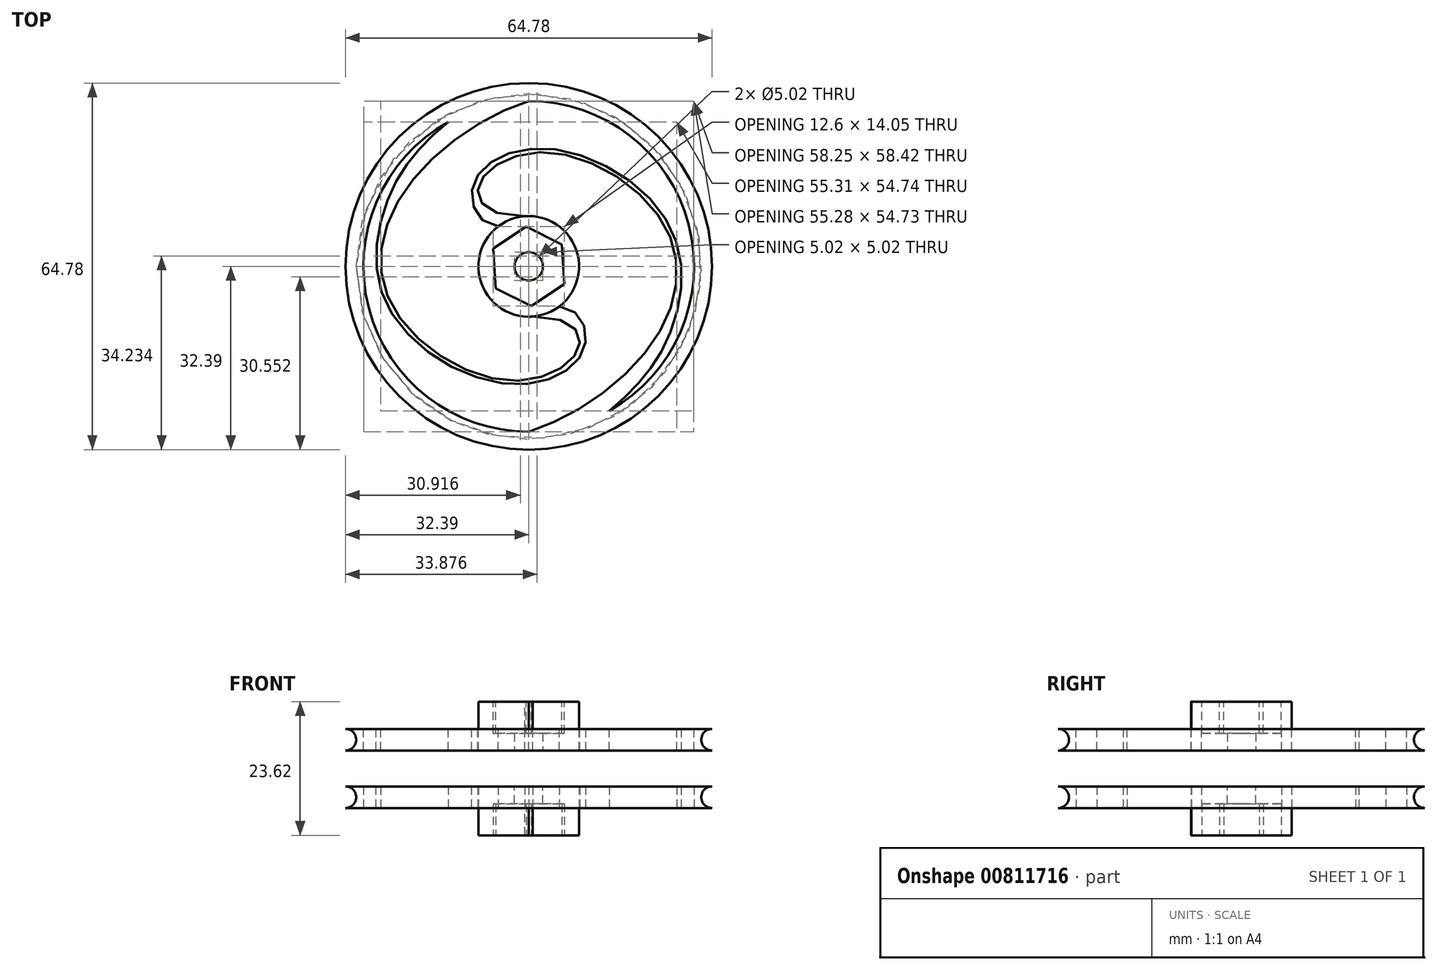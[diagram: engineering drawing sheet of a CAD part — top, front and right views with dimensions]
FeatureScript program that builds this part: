
annotation { "Feature Type Name" : "Feature", "Feature Type Description" : "" }
export const myFeature = defineFeature(function(context is Context, id is Id, definition is map)
    precondition{}
    {
        {
            var Q0;
            Q0=qCreatedBy(makeId("Front.planeOp"),FACE);
            var sketch = newSketch(context, id + "F0", { "sketchPlane" : qUnion([Q0])});
            skLineSegment(sketch, "E0.bottom", {"start": v(-32.39, 0) * mm, "end": v(0, 0) * mm, "construction": true});
            skLineSegment(sketch, "E0.top", {"start": v(-32.39, 1.9) * mm, "end": v(0, 1.9) * mm});
            skLineSegment(sketch, "E0.left", {"start": v(-32.39, 0) * mm, "end": v(-32.39, 1.9) * mm, "construction": true});
            skLineSegment(sketch, "E0.right", {"start": v(0, 0) * mm, "end": v(0, 1.9) * mm});
            skArc(sketch, "E1", {"start": v(-30.48, 0) * mm, "mid": v(-31.04, 1.35) * mm, "end": v(-32.39, 1.9) * mm});
            skArc(sketch, "E2.MirrorCS", {"start": v(-30.48, 0) * mm, "mid": v(-31.04, -1.35) * mm, "end": v(-32.39, -1.9) * mm});
            skLineSegment(sketch, "E3.MirrorCS", {"start": v(-32.39, -1.9) * mm, "end": v(0, -1.9) * mm});
            skLineSegment(sketch, "E4.MirrorCS", {"start": v(0, 0) * mm, "end": v(0, -1.9) * mm});
            skSolve(sketch);
        }
        {
            var Q0;
            Q0=qCreatedBy(makeId("Top.planeOp"),FACE);
            var sketch = newSketch(context, id + "F1", { "sketchPlane" : qUnion([Q0])});
            skCircle(sketch, "E5", {"center": v(0, 0) * mm, "radius": 30.48 * mm});
            skCircle(sketch, "E6", {"center": v(0, 0) * mm, "radius": 29.21 * mm});
            skCircle(sketch, "E7", {"center": v(0, 0) * mm, "radius": 8.9 * mm});
            skLineSegment(sketch, "E8", {"start": v(0, 0) * mm, "end": v(-39.84, 0) * mm, "construction": true});
            skLineSegment(sketch, "E9", {"start": v(0, 0) * mm, "end": v(0, -20.18) * mm, "construction": true});
            skLineSegment(sketch, "E10", {"start": v(0, 0) * mm, "end": v(39.29, -39.29) * mm, "construction": true});
            skPoint(sketch, "E11.1.internal.snap0", {"position": v(0, -10.1) * mm});
            skFitSpline(sketch, "E12", {"points": [v(0, -8.9) * mm, v(8.86, -14.27) * mm, v(-2.93, -20.18) * mm, v(-24.22, -6.82) * mm, v(-22.18, 13) * mm, v(0, 29.21) * mm], "startDerivative": vector(146.39, 8) * mm, "endDerivative": vector(99.85, 31.23) * mm});
            skFitSpline(sketch, "E13", {"points": [v(5.39, -7.07) * mm, v(9.85, -14.27) * mm, v(-2.93, -20.82) * mm, v(-25.06, -6.82) * mm, v(-24.22, 13.43) * mm, v(-14.19, 25.53) * mm], "startDerivative": vector(78.41, -4.44) * mm, "endDerivative": vector(66.4, 55.3) * mm});
            skFitSpline(sketch, "E14", {"points": [v(0.02, 8.89) * mm, v(-8.84, 14.28) * mm, v(2.95, 20.19) * mm, v(24.24, 6.83) * mm, v(22.2, -13) * mm, v(0.02, -29.2) * mm], "startDerivative": vector(-146.39, -8) * mm, "endDerivative": vector(-99.85, -31.23) * mm});
            skFitSpline(sketch, "E15", {"points": [v(-5.37, 7.09) * mm, v(-9.83, 14.28) * mm, v(2.95, 20.82) * mm, v(25.09, 6.83) * mm, v(24.24, -13.43) * mm, v(14.2, -25.52) * mm], "startDerivative": vector(-78.41, 4.44) * mm, "endDerivative": vector(-66.4, -55.3) * mm});
            skSolve(sketch);
        }
        {
            var Q0;
            Q0=makeQuery(id+"F0.imprint","IMPRINT",FACE,{"disambiguationData":[TD([[makeQuery(id+"F0.imprint","IMPRINT",EDGE,{"derivedFrom":sQuery(id+"F0.wireOp",EDGE,"E0.top")}),-1.0]])]});
            var Q1;
            Q1=sQuery(id+"F0.wireOp",EDGE,"E0.right");
            revolve(context, id + "F2", {"entities" : qUnion([Q0]), "axis" : qUnion([Q1]), "revolveType" : RevolveType.FULL, "surfaceOperationType" : NewSurfaceOperationType.NEW});
        }
        {
            var Q0;
            {var subQ6=sQuery(id+"F1.wireOp",EDGE,"E15");Q0=makeQuery(id+"F1.imprint","IMPRINT",FACE,{"disambiguationData":[TD([[makeQuery(id+"F1.imprint","IMPRINT",EDGE,{"derivedFrom":subQ6}),1.0]])]});}
            var Q1;
            {var subQ0=sQuery(id+"F1.wireOp",EDGE,"E13");Q1=makeQuery(id+"F1.imprint","IMPRINT",FACE,{"disambiguationData":[TD([[makeQuery(id+"F1.imprint","IMPRINT",EDGE,{"derivedFrom":subQ0}),1.0]])]});}
            extrude(context, id + "F3", {"entities" : qUnion([Q0, Q1]), "operationType" : NewBodyOperationType.REMOVE, "oppositeDirection" : true, "depth" : 25.4 * mm, "offsetDistance" : 25.4 * mm, "symmetric" : true});
        }
        {
            var Q0;
            {var subQ0=sQuery(id+"F1.wireOp",EDGE,"E7");var subQ48=makeQuery(id+"F1.imprint","INTERSECT",VERTEX,{"derivedFrom":[subQ0,sQuery(id+"F1.wireOp",EDGE,"01417a5a-3fe0-4376-9868-93c7ef9975e0.4.36.0")]});Q0=makeQuery(id+"F1.imprint","IMPRINT",FACE,{"disambiguationData":[TD([[makeQuery(id+"F1.imprint","IMPRINT",EDGE,{"disambiguationData":[TD([[subQ48,-1.0]])],"derivedFrom":subQ0}),1.0]])]});}
            extrude(context, id + "F4", {"entities" : qUnion([Q0]), "operationType" : NewBodyOperationType.ADD, "depth" : 6.73 * mm, "offsetDistance" : 25.4 * mm});
        }
        {
            var Q0;
            Q0=makeQuery(id+"F4.opExtrude","CAP_FACE",FACE,{"disambiguationData":[OSD([sQuery(id+"F1.wireOp",EDGE,"E7")])],"isStart":false});
            var sketch = newSketch(context, id + "F5", { "sketchPlane" : qUnion([Q0])});
            skCircle(sketch, "E16.cCircle", {"center": v(0, 0) * mm, "radius": 6.1 * mm, "construction": true});
            skLineSegment(sketch, "E16.0", {"start": v(-0.43, 7.03) * mm, "end": v(5.87, 3.89) * mm});
            skLineSegment(sketch, "E16.1", {"start": v(5.87, 3.89) * mm, "end": v(6.3, -3.14) * mm});
            skLineSegment(sketch, "E16.2", {"start": v(6.3, -3.14) * mm, "end": v(0.43, -7.03) * mm});
            skLineSegment(sketch, "E16.3", {"start": v(0.43, -7.03) * mm, "end": v(-5.87, -3.89) * mm});
            skLineSegment(sketch, "E16.4", {"start": v(-5.87, -3.89) * mm, "end": v(-6.3, 3.14) * mm});
            skLineSegment(sketch, "E16.5", {"start": v(-6.3, 3.14) * mm, "end": v(-0.43, 7.03) * mm});
            skPoint(sketch, "E16.0.midPoint", {"position": v(2.72, 5.46) * mm});
            skSolve(sketch);
        }
        {
            var Q0;
            Q0=makeQuery(id+"F5.imprint","IMPRINT",FACE,{"disambiguationData":[TD([[makeQuery(id+"F5.imprint","IMPRINT",EDGE,{"derivedFrom":sQuery(id+"F5.wireOp",EDGE,"E16.0")}),-1.0]])]});
            extrude(context, id + "F6", {"entities" : qUnion([Q0]), "operationType" : NewBodyOperationType.REMOVE, "oppositeDirection" : true, "depth" : 5.6 * mm, "offsetDistance" : 25.4 * mm});
        }
        {
            var Q0;
            Q0=makeQuery(id+"F2.opRevolve","SWEPT_FACE",FACE,{"disambiguationData":[OSD([sQuery(id+"F0.wireOp",EDGE,"E3.MirrorCS")])]});
            var sketch = newSketch(context, id + "F7", { "sketchPlane" : qUnion([Q0])});
            skCircle(sketch, "E17", {"center": v(0, 0) * mm, "radius": 2.5 * mm});
            skSolve(sketch);
        }
        {
            var Q0;
            Q0=qCreatedBy(makeId("Top.planeOp"),FACE);
            cPlane(context, id + "F8", {"entities" : qUnion([Q0]), "cplaneType" : CPlaneType.OFFSET, "offset" : 5.08 * mm, "oppositeDirection" : true, "width" : 152.4 * mm, "height" : 152.4 * mm});
        }
        {
            var Q0;
            Q0 = qSketchRegion(id + "F7", true);
            var Q1;
            Q1=sQuery(id+"F7.wireOp",EDGE,"E17");
            extrude(context, id + "F9", {"entities" : qUnion([Q0]), "operationType" : NewBodyOperationType.REMOVE, "surfaceEntities" : qUnion([Q1]), "oppositeDirection" : true, "depth" : 30.73 * mm, "offsetDistance" : 25.4 * mm});
        }
        {
            var Q0;
            Q0=makeQuery(id+"F2.opRevolve","SWEPT_BODY",BODY,{"disambiguationData":[OSD([sQuery(id+"F0.wireOp",EDGE,"E0.top"),sQuery(id+"F0.wireOp",EDGE,"E0.right"),sQuery(id+"F0.wireOp",EDGE,"E1"),sQuery(id+"F0.wireOp",EDGE,"E2.MirrorCS"),sQuery(id+"F0.wireOp",EDGE,"E3.MirrorCS"),sQuery(id+"F0.wireOp",EDGE,"E4.MirrorCS")])]});
            var Q1;
            Q1=qCreatedBy(id+"F8.planeOp",FACE);
            mirror(context, id + "F10", {"entities" : qUnion([Q0]), "mirrorPlane" : qUnion([Q1])});
        }
    });
